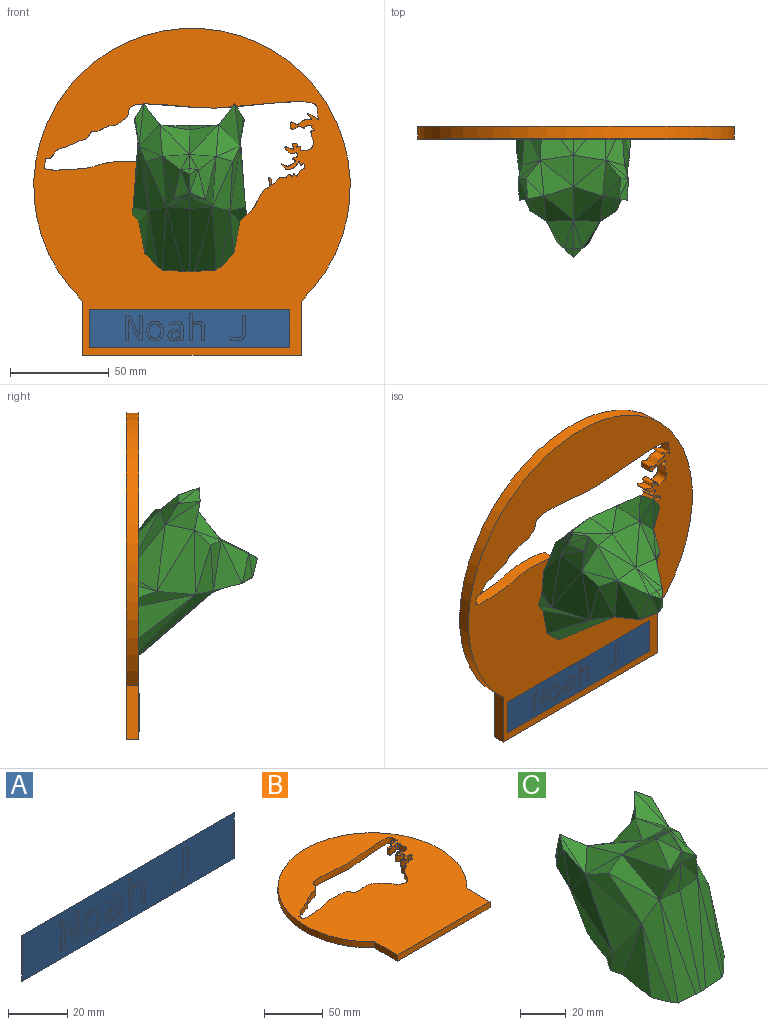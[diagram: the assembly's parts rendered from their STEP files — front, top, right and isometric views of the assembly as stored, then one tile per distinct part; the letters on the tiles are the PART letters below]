
ASSEMBLY  parts=3 mates=2
PART A: 87 faces, bbox 101.6x0.1x19.1 mm
  f0: plane 101.6x19.05mm, normal (0,-1,0), area 1693mm2, adj f1,f2,f3,f4,f6,f7,f8,f9
  f1: plane 101.6x0.03mm, normal (0,0,-1), area 2.6mm2, adj f0,f2,f4,f5
  f2: plane 19.05x0.03mm, normal (1,0,0), area 0.5mm2, adj f0,f1,f3,f5
  f3: plane 101.6x0.03mm, normal (0,0,1), area 2.6mm2, adj f0,f2,f4,f5
  f4: plane 19.05x0.03mm, normal (-1,0,0), area 0.5mm2, adj f0,f1,f3,f5
  f5: plane 101.6x19.05mm, normal (0,1,0), area 1935.5mm2, adj f1,f2,f3,f4
  f6: plane 1.86x0.03mm, normal (0,0,-1), area 0mm2, adj f0,f7,f19,f20
  f7: plane 12.66x0.03mm, normal (1,0,0), area 0.3mm2, adj f0,f6,f8,f20
  f8: plane 1.51x0.03mm, normal (0,0,1), area 0mm2, adj f0,f7,f9,f20
  f9: plane 6.92x0.03mm, normal (-1,0,0), area 0.2mm2, adj f0,f8,f10,f20
  f10: extruded ~3.5x0.12mm, area 0.1mm2, adj f0,f9,f11,f20
  f11: plane 0.05x0.03mm, normal (0,0,1), area 0mm2, adj f0,f10,f12,f20
  f12: plane 10.42x5mm, normal (0.9,0,0.43), area 0.3mm2, adj f0,f11,f13,f20
  f13: plane 1.84x0.03mm, normal (0,0,1), area 0mm2, adj f0,f12,f14,f20
  f14: plane 12.66x0.03mm, normal (-1,0,0), area 0.3mm2, adj f0,f13,f15,f20
  f15: plane 1.49x0.03mm, normal (0,0,-1), area 0mm2, adj f0,f14,f16,f20
  f16: plane 6.86x0.03mm, normal (1,0,0), area 0.2mm2, adj f0,f15,f17,f20
  f17: extruded ~3.61x0.16mm, area 0.1mm2, adj f0,f16,f18,f20
  f18: plane 0.07x0.03mm, normal (0,0,-1), area 0mm2, adj f0,f17,f19,f20
  f19: plane 10.47x5.02mm, normal (-0.9,0,-0.43), area 0.3mm2, adj f0,f6,f18,f20
  f20: plane 12.66x8.28mm, normal (0,-1,0), area 53.7mm2, adj f6,f7,f8,f9,f10,f11,f12,f13
  f21: extruded ~3.64x2.68mm, area 0.1mm2, adj f22,f32,f33,f34
  f22: extruded ~3.64x2.69mm, area 0.1mm2, adj f21,f23,f33,f34
  f23: extruded ~3.6x2.68mm, area 0.1mm2, adj f22,f32,f33,f34
  f24: extruded ~3.08x1.35mm, area 0.1mm2, adj f0,f25,f31,f33
  f25: extruded ~3.16x1.33mm, area 0.1mm2, adj f0,f24,f26,f33
  f26: extruded ~3.62x1.19mm, area 0.1mm2, adj f0,f25,f27,f33
  f27: extruded ~3.57x1.2mm, area 0.1mm2, adj f0,f26,f28,f33
  f28: extruded ~3.09x1.34mm, area 0.1mm2, adj f0,f27,f29,f33
  f29: extruded ~3.16x1.32mm, area 0.1mm2, adj f0,f28,f30,f33
  f30: extruded ~3.59x1.17mm, area 0.1mm2, adj f0,f29,f31,f33
  f31: extruded ~3.6x1.21mm, area 0.1mm2, adj f0,f24,f30,f33
  f32: extruded ~3.6x2.7mm, area 0.1mm2, adj f21,f23,f33,f34
  f33: plane 9.85x8.63mm, normal (0,-1,0), area 36.4mm2, adj f21,f22,f23,f24,f25,f26,f27,f28
  f34: plane 7.24x5.38mm, normal (0,-1,0), area 32.4mm2, adj f21,f22,f23,f32
  f35: plane 1.4x0.06mm, normal (0.04,0,-1), area 0mm2, adj f36,f58,f59,f60
  f36: plane 0.86x0.03mm, normal (-1,0,0), area 0mm2, adj f35,f37,f59,f60
  f37: extruded ~1.99x0.76mm, area 0.1mm2, adj f36,f38,f59,f60
  f38: extruded ~2.03x0.71mm, area 0.1mm2, adj f37,f39,f59,f60
  f39: extruded ~1.73x1.54mm, area 0.1mm2, adj f38,f40,f59,f60
  f40: extruded ~1.42x0.71mm, area 0mm2, adj f39,f58,f59,f60
  f41: plane 1.32x0.32mm, normal (-0.97,0,-0.24), area 0mm2, adj f0,f42,f57,f59
  f42: plane 1.13x0.03mm, normal (0,0,-1), area 0mm2, adj f0,f41,f43,f59
  f43: plane 6.51x0.03mm, normal (1,0,0), area 0.2mm2, adj f0,f42,f44,f59
  f44: extruded ~2.42x0.88mm, area 0.1mm2, adj f0,f43,f45,f59
  f45: extruded ~2.84x0.75mm, area 0.1mm2, adj f0,f44,f46,f59
  f46: extruded ~3.32x0.83mm, area 0.1mm2, adj f0,f45,f47,f59
  f47: plane 1.19x0.55mm, normal (-0.91,0,-0.42), area 0mm2, adj f0,f46,f48,f59
  f48: extruded ~2.84x0.71mm, area 0.1mm2, adj f0,f47,f49,f59
  f49: extruded ~2.11x2.04mm, area 0.1mm2, adj f0,f48,f50,f59
  f50: plane 0.6x0.03mm, normal (-1,0,0), area 0mm2, adj f0,f49,f51,f59
  f51: plane 1.76x0.06mm, normal (-0.03,0,1), area 0mm2, adj f0,f50,f52,f59
  f52: extruded ~4.42x3.01mm, area 0.2mm2, adj f0,f51,f53,f59
  f53: extruded ~2.09x0.8mm, area 0.1mm2, adj f0,f52,f54,f59
  f54: extruded ~2.21x0.75mm, area 0.1mm2, adj f0,f53,f55,f59
  f55: extruded ~1.81x0.33mm, area 0mm2, adj f0,f54,f56,f59
  f56: extruded ~1.37x1.16mm, area 0mm2, adj f0,f55,f57,f59
  f57: plane 0.07x0.03mm, normal (0,0,-1), area 0mm2, adj f0,f41,f56,f59
  f58: extruded ~2.41x0.53mm, area 0.1mm2, adj f35,f40,f59,f60
  f59: plane 9.85x7.71mm, normal (0,-1,0), area 38.5mm2, adj f35,f36,f37,f38,f39,f40,f41,f42
  f60: plane 4.52x3.55mm, normal (0,-1,0), area 12.9mm2, adj f35,f36,f37,f38,f39,f40,f58
  f61: plane 6.12x0.03mm, normal (-1,0,0), area 0.2mm2, adj f0,f62,f74,f75
  f62: plane 1.58x0.03mm, normal (0,0,-1), area 0mm2, adj f0,f61,f63,f75
  f63: plane 6.21x0.03mm, normal (1,0,0), area 0.2mm2, adj f0,f62,f64,f75
  f64: extruded ~3.47x3.37mm, area 0.1mm2, adj f0,f63,f65,f75
  f65: extruded ~2.91x1.45mm, area 0.1mm2, adj f0,f64,f66,f75
  f66: plane 0.09x0.03mm, normal (0,0,1), area 0mm2, adj f0,f65,f67,f75
  f67: plane 1.25x0.07mm, normal (1,0,-0.06), area 0mm2, adj f0,f66,f68,f75
  f68: plane 4x0.03mm, normal (1,0,0), area 0.1mm2, adj f0,f67,f69,f75
  f69: plane 1.58x0.03mm, normal (0,0,1), area 0mm2, adj f0,f68,f70,f75
  f70: plane 13.47x0.03mm, normal (-1,0,0), area 0.3mm2, adj f0,f69,f71,f75
  f71: plane 1.58x0.03mm, normal (0,0,-1), area 0mm2, adj f0,f70,f72,f75
  f72: plane 4.93x0.03mm, normal (1,0,0), area 0.1mm2, adj f0,f71,f73,f75
  f73: extruded ~3.45x2.66mm, area 0.1mm2, adj f0,f72,f74,f75
  f74: extruded ~2.25x2.06mm, area 0.1mm2, adj f0,f61,f73,f75
  f75: plane 13.47x7.87mm, normal (0,-1,0), area 41.8mm2, adj f61,f62,f63,f64,f65,f66,f67,f68
  f76: plane 1.44x0.03mm, normal (-1,0,0), area 0mm2, adj f0,f77,f85,f86
  f77: extruded ~2.81x0.51mm, area 0.1mm2, adj f0,f76,f78,f86
  f78: extruded ~3.27x1.1mm, area 0.1mm2, adj f0,f77,f79,f86
  f79: extruded ~2.97x1.22mm, area 0.1mm2, adj f0,f78,f80,f86
  f80: plane 8.75x0.03mm, normal (1,0,0), area 0.2mm2, adj f0,f79,f81,f86
  f81: plane 1.61x0.03mm, normal (0,0,1), area 0mm2, adj f0,f80,f82,f86
  f82: plane 8.77x0.03mm, normal (-1,0,0), area 0.2mm2, adj f0,f81,f83,f86
  f83: extruded ~1.96x0.8mm, area 0.1mm2, adj f0,f82,f84,f86
  f84: extruded ~2.2x0.69mm, area 0.1mm2, adj f0,f83,f85,f86
  f85: extruded ~2.68x0.54mm, area 0.1mm2, adj f0,f76,f84,f86
  f86: plane 12.83x7.29mm, normal (0,-1,0), area 26.8mm2, adj f76,f77,f78,f79,f80,f81,f82,f83
PART B: 7 faces, bbox 160.5x165.8x6.4 mm
  f0: plane 165.84x160.5mm, normal (0,0,-1), area 19991.7mm2, adj f1,f2,f3,f4,f6
  f1: plane 27.56x6.35mm, normal (1,0,0), area 175mm2, adj f0,f2,f4,f5
  f2: cylinder r=80.25mm len=160.5mm, axis (0,0,-1), area 2424.7mm2, adj f0,f1,f3,f5
  f3: plane 27.56x6.35mm, normal (-1,0,0), area 175mm2, adj f0,f2,f4,f5
  f4: plane 110.87x6.35mm, normal (0,-1,0), area 704mm2, adj f0,f1,f3,f5
  f5: plane 165.84x160.5mm, normal (0,0,1), area 19991.7mm2, adj f1,f2,f3,f4,f6
  f6: extruded ~138.02x55.89mm, area 2585.5mm2, adj f0,f5
PART C: 91 faces, bbox 58.1x65.4x75.3 mm
  f0: plane 9.47x6.02mm, normal (-0.89,0.44,0.1), area 27.9mm2, adj f1,f18,f90
  f1: plane 8.22x7.13mm, normal (-0.97,0.13,-0.18), area 11.2mm2, adj f0,f12,f90
  f2: plane 10.92x10.09mm, normal (0.74,0.67,0), area 70.5mm2, adj f4,f7,f35
  f3: plane 21.07x6.78mm, normal (-0.97,-0.24,-0.03), area 55.9mm2, adj f6,f9,f13
  f4: plane 12.8x4.94mm, normal (-0.75,0.64,0.15), area 30.7mm2, adj f2,f6,f8
  f5: plane 18.52x11.22mm, normal (0.35,-0.52,0.78), area 40.6mm2, adj f6,f13,f35
  f6: plane 12.8x6.38mm, normal (-0.84,0.49,0.22), area 44.5mm2, adj f3,f4,f5
  f7: plane 16.56x10.09mm, normal (0.65,0.72,0.25), area 100.5mm2, adj f2,f8,f21
  f8: plane 11.55x11.37mm, normal (-0.5,0.71,-0.5), area 41.1mm2, adj f4,f7,f9
  f9: plane 11.37x10.63mm, normal (-0.52,0.67,-0.53), area 75.7mm2, adj f3,f8,f11
  f10: plane 18.38x13.96mm, normal (-0.74,0.62,-0.27), area 62.8mm2, adj f11,f19,f90
  f11: plane 20.15x17.75mm, normal (-0.58,0.72,-0.39), area 165mm2, adj f9,f10,f12,f90
  f12: plane 28.86x24.29mm, normal (-0.98,0.17,-0.13), area 248.9mm2, adj f1,f11,f14,f90
  f13: plane 21.07x12.14mm, normal (-0.99,-0.1,-0.05), area 114.3mm2, adj f3,f5,f14
  f14: plane 30.38x28.86mm, normal (-1,0.05,0.06), area 257.8mm2, adj f12,f13,f39
  f15: plane 47.76x15.25mm, normal (-0.46,-0.85,0.25), area 296.1mm2, adj f16,f38,f44,f90
  f16: plane 37.84x13.58mm, normal (-0.62,-0.76,0.2), area 150.8mm2, adj f15,f17,f90
  f17: plane 35.07x14.47mm, normal (-0.96,-0.25,0.11), area 237mm2, adj f16,f18,f90
  f18: plane 28.33x10.81mm, normal (-0.76,-0.65,-0.02), area 132.9mm2, adj f0,f17,f39,f90
  f19: plane 16.59x14.73mm, normal (-0.1,0.92,-0.38), area 194.2mm2, adj f10,f20,f30,f90
  f20: plane 16.59x13.49mm, normal (0.03,0.84,0.54), area 133.4mm2, adj f19,f21,f51
  f21: plane 16.59x16.56mm, normal (0.17,0.91,0.39), area 141.3mm2, adj f7,f20,f23
  f22: plane 11.66x6.42mm, normal (-0.74,-0.43,0.52), area 33.1mm2, adj f24,f25,f53
  f23: plane 18.89x14.92mm, normal (0.32,0.46,0.83), area 165.6mm2, adj f21,f26,f55
  f24: plane 4.45x4.43mm, normal (-0.09,0.55,0.83), area 11.8mm2, adj f22,f27,f54
  f25: plane 12.18x9.33mm, normal (-0.52,-0.41,0.75), area 65mm2, adj f22,f28,f31
  f26: plane 20.04x14.92mm, normal (-0.01,0.23,0.97), area 141.1mm2, adj f23,f29,f37
  f27: plane 13.15x10.02mm, normal (-0.1,0.62,0.78), area 36mm2, adj f24,f29,f57
  f28: plane 24.18x9.78mm, normal (-0.82,-0.18,0.55), area 141.5mm2, adj f25,f29,f34
  f29: plane 13.61x13.15mm, normal (-0.05,0.61,0.79), area 109.8mm2, adj f26,f27,f28
  f30: plane 11.67x6.33mm, normal (-0.02,0.91,-0.42), area 40.5mm2, adj f19,f61,f90
  f31: plane 8.12x6.14mm, normal (0.56,0.27,-0.78), area 2.4mm2, adj f25,f32,f70
  f32: plane 8.12x6.17mm, normal (0.16,-0.99,-0.06), area 25.4mm2, adj f31,f33,f71
  f33: plane 14.85x11.71mm, normal (0.16,-0.96,-0.22), area 62.6mm2, adj f32,f34,f42
  f34: plane 24.18x14.85mm, normal (-0.96,-0.21,0.19), area 186.7mm2, adj f28,f33,f36
  f35: plane 18.52x11.22mm, normal (0.05,-0.52,0.85), area 102.1mm2, adj f2,f5,f37
  f36: plane 21.44x14.4mm, normal (-0.5,-0.51,0.7), area 128.1mm2, adj f34,f38,f40
  f37: plane 20.04x12.08mm, normal (-0.55,0.16,0.82), area 139.4mm2, adj f26,f35,f40
  f38: plane 21.44x17.61mm, normal (-0.67,-0.53,0.53), area 160.2mm2, adj f15,f36,f41
  f39: plane 30.38x29.75mm, normal (-0.92,-0.28,0.27), area 345.2mm2, adj f14,f18,f41
  f40: plane 12.08x10.43mm, normal (-0.57,0.12,0.81), area 53.6mm2, adj f36,f37,f41
  f41: plane 29.75x17.61mm, normal (-0.95,-0.25,0.2), area 140.1mm2, adj f38,f39,f40
  f42: plane 15.59x11.71mm, normal (-0.06,-1,-0.05), area 91.5mm2, adj f33,f43,f73
  f43: plane 48.08x13.85mm, normal (-0.03,-0.96,0.27), area 360.7mm2, adj f42,f44,f74,f90
  f44: plane 48.02x13.73mm, normal (-0.05,-0.96,0.27), area 261.4mm2, adj f15,f43,f90
  f45: plane 10.92x10.09mm, normal (-0.74,0.67,0), area 70.5mm2, adj f46,f62,f77
  f46: plane 12.8x4.94mm, normal (0.75,0.64,0.15), area 30.7mm2, adj f45,f49,f63
  f47: plane 21.07x6.78mm, normal (0.97,-0.24,-0.03), area 55.9mm2, adj f49,f64,f68
  f48: plane 18.52x11.22mm, normal (-0.35,-0.52,0.78), area 40.6mm2, adj f49,f68,f77
  f49: plane 12.8x6.38mm, normal (0.84,0.49,0.22), area 44.5mm2, adj f46,f47,f48
  f50: plane 16.59x14.73mm, normal (0.1,0.92,-0.38), area 194.2mm2, adj f51,f61,f65,f90
  f51: plane 16.59x13.49mm, normal (-0.03,0.84,0.54), area 133.4mm2, adj f20,f50,f52
  f52: plane 16.59x16.56mm, normal (-0.17,0.91,0.39), area 141.3mm2, adj f51,f55,f62
  f53: plane 11.66x6.42mm, normal (0.74,-0.43,0.52), area 33.1mm2, adj f22,f54,f56
  f54: plane 4.45x4.43mm, normal (0.09,0.55,0.83), area 11.8mm2, adj f24,f53,f57
  f55: plane 18.89x14.92mm, normal (-0.32,0.46,0.83), area 165.6mm2, adj f23,f52,f58
  f56: plane 12.18x9.33mm, normal (0.52,-0.41,0.75), area 65mm2, adj f53,f59,f70
  f57: plane 13.15x10.02mm, normal (0.1,0.62,0.78), area 36mm2, adj f27,f54,f60
  f58: plane 20.04x14.92mm, normal (0.01,0.23,0.97), area 141.1mm2, adj f55,f60,f79
  f59: plane 24.18x9.78mm, normal (0.82,-0.18,0.55), area 141.5mm2, adj f56,f60,f76
  f60: plane 13.61x13.15mm, normal (0.05,0.61,0.79), area 109.8mm2, adj f57,f58,f59
  f61: plane 11.67x6.33mm, normal (0.02,0.91,-0.42), area 40.5mm2, adj f30,f50,f90
  f62: plane 16.56x10.09mm, normal (-0.65,0.72,0.25), area 100.5mm2, adj f45,f52,f63
  f63: plane 11.55x11.37mm, normal (0.5,0.71,-0.5), area 41.1mm2, adj f46,f62,f64
  f64: plane 11.37x10.63mm, normal (0.52,0.67,-0.53), area 75.7mm2, adj f47,f63,f66
  f65: plane 18.38x13.96mm, normal (0.74,0.62,-0.27), area 62.8mm2, adj f50,f66,f90
  f66: plane 20.15x17.75mm, normal (0.58,0.72,-0.39), area 165mm2, adj f64,f65,f67,f90
  f67: plane 28.86x24.29mm, normal (0.98,0.17,-0.13), area 248.9mm2, adj f66,f69,f85,f90
  f68: plane 21.07x12.14mm, normal (0.99,-0.1,-0.05), area 114.3mm2, adj f47,f48,f69
  f69: plane 30.38x28.86mm, normal (1,0.05,0.06), area 257.8mm2, adj f67,f68,f80
  f70: plane 8.12x6.14mm, normal (-0.56,0.27,-0.78), area 2.4mm2, adj f31,f56,f71
  f71: plane 8.12x6.17mm, normal (-0.16,-0.99,-0.06), area 25.4mm2, adj f32,f70,f72
  f72: plane 14.85x11.71mm, normal (-0.16,-0.96,-0.22), area 62.6mm2, adj f71,f73,f76
  f73: plane 15.59x11.71mm, normal (0.06,-1,-0.05), area 91.5mm2, adj f42,f72,f74
  f74: plane 48.08x13.85mm, normal (0.03,-0.96,0.27), area 360.7mm2, adj f43,f73,f75,f90
  f75: plane 48.02x13.73mm, normal (0.05,-0.96,0.27), area 261.4mm2, adj f74,f86,f90
  f76: plane 24.18x14.85mm, normal (0.96,-0.21,0.19), area 186.7mm2, adj f59,f72,f78
  f77: plane 18.52x11.22mm, normal (-0.05,-0.52,0.85), area 102.1mm2, adj f45,f48,f79
  f78: plane 21.44x14.4mm, normal (0.5,-0.51,0.7), area 128.1mm2, adj f76,f81,f82
  f79: plane 20.04x12.08mm, normal (0.55,0.16,0.82), area 139.4mm2, adj f58,f77,f82
  f80: plane 30.38x29.75mm, normal (0.92,-0.28,0.27), area 345.2mm2, adj f69,f83,f89
  f81: plane 21.44x17.61mm, normal (0.67,-0.53,0.53), area 160.2mm2, adj f78,f83,f86
  f82: plane 12.08x10.43mm, normal (0.57,0.12,0.81), area 53.6mm2, adj f78,f79,f83
  f83: plane 29.75x17.61mm, normal (0.95,-0.25,0.2), area 140.1mm2, adj f80,f81,f82
  f84: plane 9.47x6.02mm, normal (0.89,0.44,0.1), area 27.9mm2, adj f85,f89,f90
  f85: plane 8.22x7.13mm, normal (0.97,0.13,-0.18), area 11.2mm2, adj f67,f84,f90
  f86: plane 47.76x15.25mm, normal (0.46,-0.85,0.25), area 296.1mm2, adj f75,f81,f87,f90
  f87: plane 37.84x13.58mm, normal (0.62,-0.76,0.2), area 150.8mm2, adj f86,f88,f90
  f88: plane 35.07x14.47mm, normal (0.96,-0.25,0.11), area 237mm2, adj f87,f89,f90
  f89: plane 28.33x10.81mm, normal (0.76,-0.65,-0.02), area 132.9mm2, adj f80,f84,f88,f90
  f90: plane 58.12x58.09mm, normal (0,0.42,-0.91), area 2936.1mm2, adj f0,f1,f10,f11,f12,f15,f16,f17
PLACE A t=(14.52,-91.8,47.34)mm
PLACE B rot(axis=(1,0,0),90deg) t=(15.89,-85.45,119.34)mm
PLACE C rot(axis=(1,0,0),65deg) t=(12.55,-35.82,100.81)mm
MATE fastened B.f5 <-> A.f5  axis (0,-1,0) through (14.52,-91.8,47.34)mm
MATE fastened C.f90 <-> B.f5  axis (0,1,0) through (14.52,-91.8,108.3)mm
